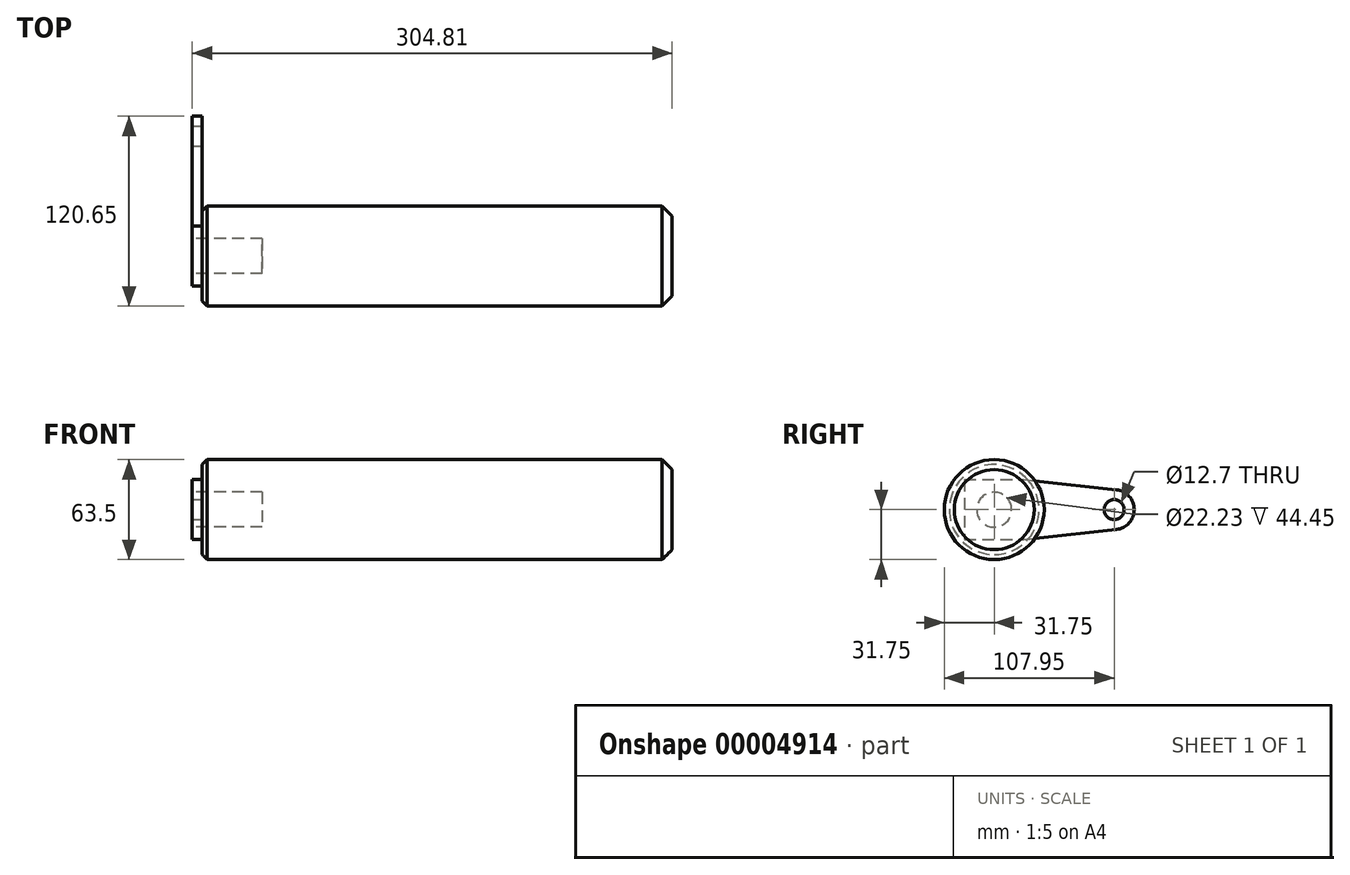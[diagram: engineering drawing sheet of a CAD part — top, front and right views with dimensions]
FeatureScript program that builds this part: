
annotation { "Feature Type Name" : "Feature", "Feature Type Description" : "" }
export const myFeature = defineFeature(function(context is Context, id is Id, definition is map)
    precondition{}
    {
        {
            var Q0;
            Q0=qCreatedBy(makeId("Right.planeOp"),FACE);
            var sketch = newSketch(context, id + "F0", { "sketchPlane" : qUnion([Q0])});
            skCircle(sketch, "E0", {"center": v(0, 0) * mm, "radius": 31.75 * mm});
            skSolve(sketch);
        }
        {
            var Q0;
            Q0=makeQuery(id+"F0.imprint","IMPRINT",FACE,{"disambiguationData":[TD([[makeQuery(id+"F0.imprint","IMPRINT",EDGE,{"derivedFrom":sQuery(id+"F0.wireOp",EDGE,"E0")}),1.0]])]});
            extrude(context, id + "F1", {"entities" : qUnion([Q0]), "endBound" : BoundingType.SYMMETRIC, "depth" : 298.45 * mm});
        }
        {
            var Q0;
            Q0=makeQuery(id+"F1.opExtrude","CAP_EDGE",EDGE,{"disambiguationData":[OSD([sQuery(id+"F0.wireOp",EDGE,"E0")])],"isStart":false});
            chamfer(context, id + "F2", {"entities" : qUnion([Q0]), "width" : 6.35 * mm, "tangentPropagation" : true});
        }
        {
            var Q0;
            Q0=makeQuery(id+"F1.opExtrude","CAP_EDGE",EDGE,{"disambiguationData":[OSD([sQuery(id+"F0.wireOp",EDGE,"E0")])],"isStart":true});
            chamfer(context, id + "F3", {"entities" : qUnion([Q0]), "width" : 3.17 * mm, "tangentPropagation" : true});
        }
        {
            var Q0;
            Q0=makeQuery(id+"F1.opExtrude","CAP_FACE",FACE,{"disambiguationData":[OSD([sQuery(id+"F0.wireOp",EDGE,"E0")])],"isStart":true});
            var sketch = newSketch(context, id + "F4", { "sketchPlane" : qUnion([Q0])});
            skLineSegment(sketch, "E1", {"start": v(0, 0) * mm, "end": v(0, 19.05) * mm, "construction": true});
            skLineSegment(sketch, "E2", {"start": v(0, 0) * mm, "end": v(-76.2, 0) * mm, "construction": true});
            skLineSegment(sketch, "E3.0", {"start": v(19.05, 0) * mm, "end": v(19.05, 19.05) * mm});
            skArc(sketch, "E4", {"start": v(-77.59, 12.62) * mm, "mid": v(-88.9, 0) * mm, "end": v(-77.59, -12.62) * mm});
            skCircle(sketch, "E5", {"center": v(-76.2, 0) * mm, "radius": 6.35 * mm});
            skLineSegment(sketch, "E6", {"start": v(19.05, 19.05) * mm, "end": v(-19.05, 19.05) * mm});
            skLineSegment(sketch, "E7", {"start": v(-19.05, 19.05) * mm, "end": v(-77.59, 12.62) * mm});
            skLineSegment(sketch, "E8.0.MirrorCS", {"start": v(-19.05, -19.05) * mm, "end": v(-77.59, -12.62) * mm});
            skLineSegment(sketch, "E9.0.MirrorCS", {"start": v(19.05, -19.05) * mm, "end": v(-19.05, -19.05) * mm});
            skLineSegment(sketch, "E10.0.MirrorCS", {"start": v(19.05, 0) * mm, "end": v(19.05, -19.05) * mm});
            skSolve(sketch);
        }
        {
            var Q0;
            {var subQ9=sQuery(id+"F4.wireOp",EDGE,"E4");Q0=qUnion([makeQuery(id+"F4.imprint","IMPRINT",FACE,{"disambiguationData":[TD([[makeQuery(id+"F4.imprint","IMPRINT",EDGE,{"derivedFrom":sQuery(id+"F4.wireOp",EDGE,"E3.0")}),1.0]])]}),makeQuery(id+"F4.imprint","IMPRINT",FACE,{"disambiguationData":[TD([[makeQuery(id+"F4.imprint","IMPRINT",EDGE,{"derivedFrom":subQ9}),1.0]])]})]);}
            extrude(context, id + "F5", {"entities" : qUnion([Q0]), "operationType" : NewBodyOperationType.ADD, "depth" : 6.35 * mm});
        }
        {
            var Q0;
            Q0=makeQuery(id+"F5.opExtrude","CAP_FACE",FACE,{"disambiguationData":[OSD([sQuery(id+"F4.wireOp",EDGE,"E3.0"),sQuery(id+"F4.wireOp",EDGE,"E4"),sQuery(id+"F4.wireOp",EDGE,"E5"),sQuery(id+"F4.wireOp",EDGE,"E6"),sQuery(id+"F4.wireOp",EDGE,"E7"),sQuery(id+"F4.wireOp",EDGE,"E8.0.MirrorCS"),sQuery(id+"F4.wireOp",EDGE,"E9.0.MirrorCS"),sQuery(id+"F4.wireOp",EDGE,"E10.0.MirrorCS")])],"isStart":false});
            var sketch = newSketch(context, id + "F6", { "sketchPlane" : qUnion([Q0])});
            skCircle(sketch, "E11", {"center": v(0, 0) * mm, "radius": 11.11 * mm});
            skSolve(sketch);
        }
        {
            var Q0;
            Q0=makeQuery(id+"F6.imprint","IMPRINT",FACE,{"disambiguationData":[TD([[makeQuery(id+"F6.imprint","IMPRINT",EDGE,{"derivedFrom":sQuery(id+"F6.wireOp",EDGE,"E11")}),1.0]])]});
            extrude(context, id + "F7", {"entities" : qUnion([Q0]), "operationType" : NewBodyOperationType.REMOVE, "oppositeDirection" : true, "depth" : 44.45 * mm});
        }
    });
